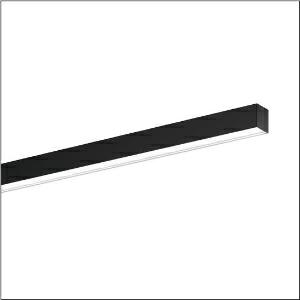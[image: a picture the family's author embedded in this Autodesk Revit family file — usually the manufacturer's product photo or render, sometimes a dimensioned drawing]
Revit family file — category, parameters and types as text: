
# Revit family: silica_r__21_51mx23tat4b_8a74
name_source: partatom
category: Lighting Fixtures
units: mm (PartAtom-declared; Revit-internal decimal feet)

## family parameters
Cut with Voids When Loaded = No
Host = Face
Light Source = No
Part Type = Normal
Room Calculation Point = No
Round Connector Dimension = Use Diameter
Shared = No

## types (1)
- --- (1 x LED, 3230 lm, 32.4 W, 6500K)
    Apparent Load = 32 VA
    CIE Flux Codes = 78 96 99 100 100
    Color Rendering = 80
    Color Temperature = 6500K
    Default Elevation = 1800 mm
    Description = Silica® 21, office luminaire, primary optical cover: prismatic diffuser, of PMMA, CAT 2 (L<= 3000cd/m²), light emission: direct distribution, primary light characteristic: symmetric, installation type: surface-mounted, LED, rated luminous flux: 3.230lm, luminous efficacy: 95lm/W, light colour: 8tw, colour temperature: 2700..6500K, control gear: ECG DALI, with terminal, 3+2-pole, max. 2.5mm², mains connection: 220..240V, AC, 50/60Hz, rated input power: 34W, luminaire housing, of aluminium, jet black (RAL 9005), length: 1.204mm, width: 53mm, height: 53mm, protection rating (complete): IP20, insulation class (complete): insulation class I (protective earthing), certification: CE, permissible operating ambient temperature: 0..+35°C, standard: EN 50419, packaging unit: 1 piece
    Height = 0 mm  [stored 0 ft]
    Lamp = 1 x LED
    Lamp Light Flux = 3230 lm
    Lamp Power = 32.4 W
    Lamp count = 1
    Length = 1204 mm
    Luminous efficacy = 100 lm/W
    Manufacturer = Siteco
    ModVariant = No
    Model = 51MX23TAT4B
    Mounting Place = Ceiling
    Mounting Type = Recessed
    Number of Poles = 1
    OnlyDefault = Yes
    Power Factor = 1
    Product Name = Silica® 21
    Product group = office luminaire | ceiling recessed
    ProductGroupID = 401
    Protection Class = Protection class I
    Protection Degree = IP 20
    RLX_Detail_Level = 1
    RLX_Emergency_Light_Flux = 0 lm
    RLX_Emergency_Type = 0
    RLX_Emergency_Type_DB = No
    RlxData = <blob elided: 20505 chars, md5=fcb0e703>
    Socket = socket
    Standby Power = 0 W
    System Light Flux = 3230 lm
    System Power = 32 W
    Type Comments = individual setting
    Type Image = l_1297760.jpg
    URL = http://relux.com
    VarID = @adj_071143
    Voltage = 0 V
    Weight = 0.00 kg
    Width = 53 mm

note: [stored X ft] marks values corroborated as IEEE doubles in the binary element streams (Revit-internal decimal feet)

## geometry (parser evidence)
native form markers: Blend x4, Sweep x10
no freeform markers — native parametric forms only
